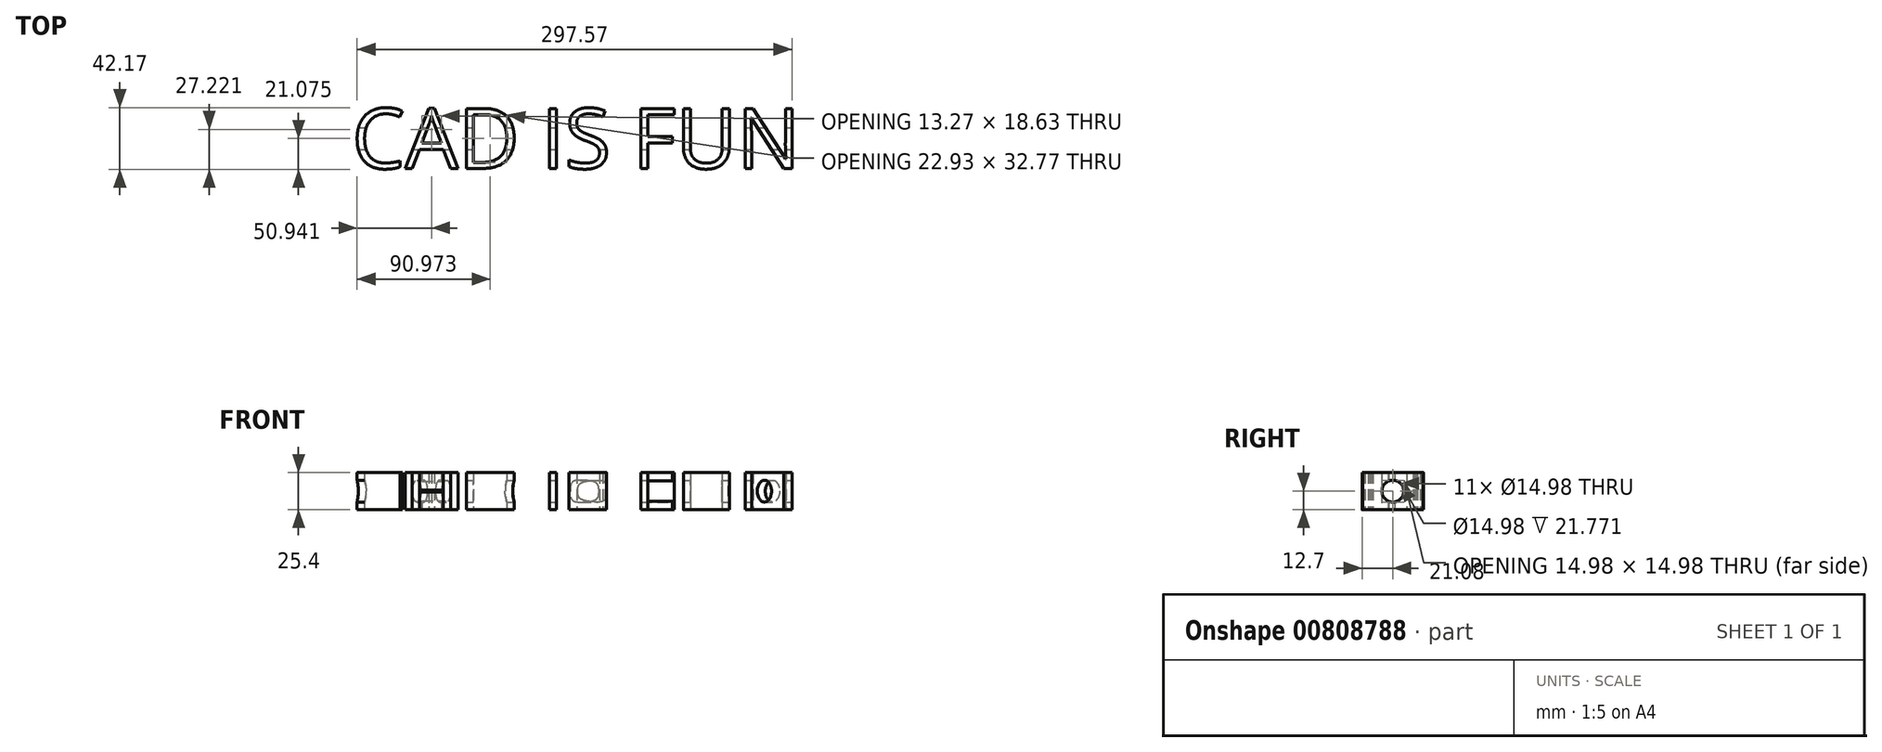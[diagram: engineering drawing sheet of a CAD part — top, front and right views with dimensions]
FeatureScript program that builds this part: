
annotation { "Feature Type Name" : "Feature", "Feature Type Description" : "" }
export const myFeature = defineFeature(function(context is Context, id is Id, definition is map)
    precondition{}
    {
        {
            var Q0;
            Q0=qCreatedBy(makeId("Top.planeOp"),FACE);
            var sketch = newSketch(context, id + "F0", { "sketchPlane" : qUnion([Q0])});
            skText(sketch, "E0", { "text": "CAD IS FUN", "fontName": "OpenSans-Regular.ttf"});
            const initialGuessF0  = {"E0": [-0.3048, -0.04137, 1, 0, 0.04137]};
            skSetInitialGuess(sketch, initialGuessF0);
            skSolve(sketch);
        }
        {
            var Q0;
            Q0 = qSketchRegion(id + "F0", true);
            extrude(context, id + "F1", {"entities" : qUnion([Q0]), "depth" : 25.4 * mm, "offsetDistance" : 25.4 * mm});
        }
        {
            var Q0;
            Q0=makeQuery(id+"F1.opExtrude","SWEPT_FACE",FACE,{"disambiguationData":[OSD([sQuery(id+"F0.wireOp",EDGE,"E0.sketch_text.stroke-109")])]});
            var sketch = newSketch(context, id + "F2", { "sketchPlane" : qUnion([Q0])});
            skCircle(sketch, "E1", {"center": v(-20.86, 12.7) * mm, "radius": 7.49 * mm});
            skPoint(sketch, "E1.centerSnap0", {"position": v(-20.86, 0) * mm});
            skSolve(sketch);
        }
        {
            var Q0;
            Q0 = qSketchRegion(id + "F2", true);
            var Q1;
            Q1=makeQuery(id+"F1.opExtrude","SWEPT_FACE",FACE,{"disambiguationData":[OSD([sQuery(id+"F0.wireOp",EDGE,"E0.sketch_text.stroke-9")])]});
            var Q2;
            Q2=makeQuery(id+"F1.opExtrude","CAP_VERTEX",VERTEX,{"disambiguationData":[OSD([sQuery(id+"F0.wireOp",EDGE,"E0.sketch_text.stroke-8"),sQuery(id+"F0.wireOp",EDGE,"E0.sketch_text.stroke-9")])],"isStart":false});
            extrude(context, id + "F3", {"entities" : qUnion([Q0]), "operationType" : NewBodyOperationType.REMOVE, "endBound" : BoundingType.THROUGH_ALL, "oppositeDirection" : true, "depth" : 25.4 * mm, "offsetDistance" : 25.4 * mm});
        }
    });
